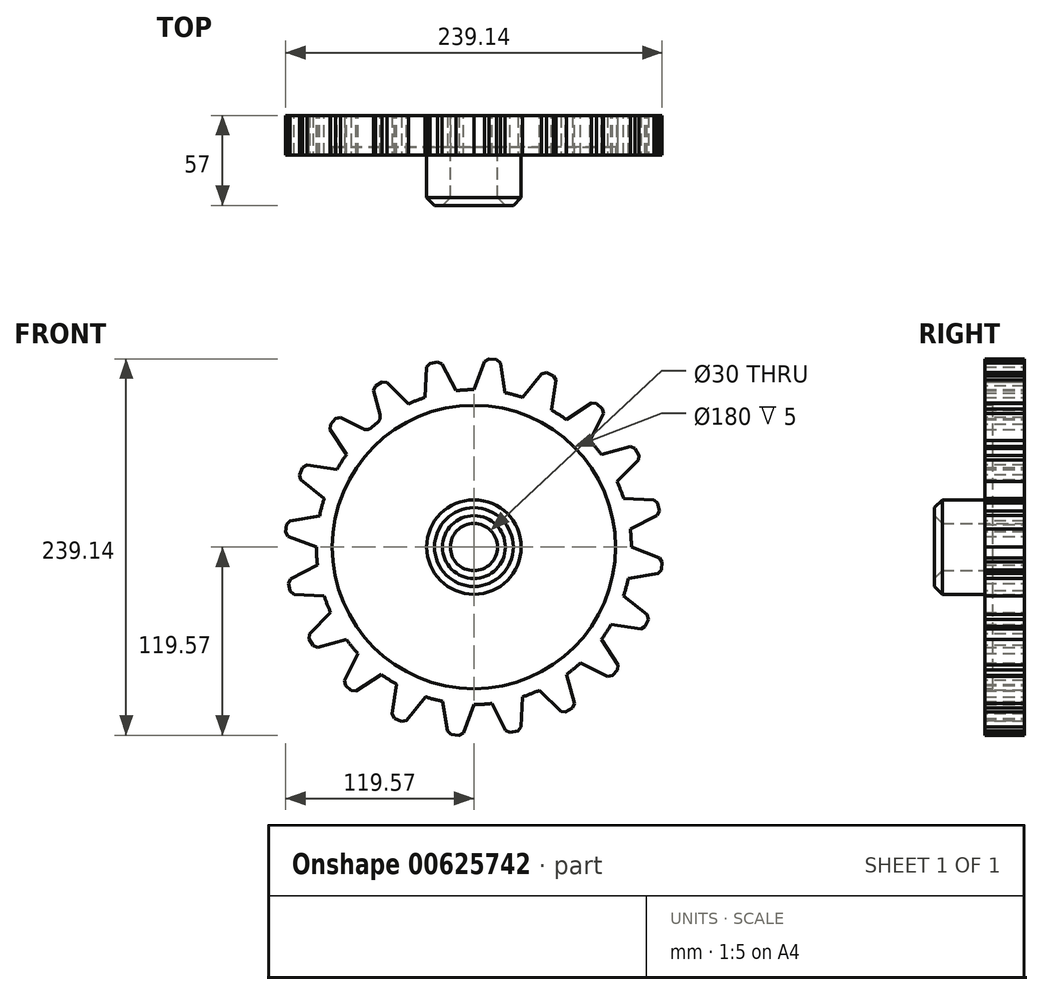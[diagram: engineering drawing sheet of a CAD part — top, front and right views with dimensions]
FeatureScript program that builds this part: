
annotation { "Feature Type Name" : "Feature", "Feature Type Description" : "" }
export const myFeature = defineFeature(function(context is Context, id is Id, definition is map)
    precondition{}
    {
        {
            var Q0;
            Q0=qCreatedBy(makeId("Front.planeOp"),FACE);
            var sketch = newSketch(context, id + "F0", { "sketchPlane" : qUnion([Q0])});
            skCircle(sketch, "E0", {"center": v(0, 0) * mm, "radius": 100 * mm});
            skCircle(sketch, "E1", {"center": v(0, 0) * mm, "radius": 120 * mm, "construction": true});
            skLineSegment(sketch, "E2", {"start": v(101.28, 64.36) * mm, "end": v(80.9, 58.79) * mm});
            skLineSegment(sketch, "E3", {"start": v(0, 0) * mm, "end": v(0, 0) * mm});
            skLineSegment(sketch, "E4.MirrorCS", {"start": v(105.82, 56.59) * mm, "end": v(90.95, 41.57) * mm});
            skLineSegment(sketch, "E5", {"start": v(101.28, 64.36) * mm, "end": v(105.82, 56.59) * mm});
            skLineSegment(sketch, "E6.1.0", {"start": v(76.44, 92.5) * mm, "end": v(58.77, 80.9) * mm});
            skLineSegment(sketch, "E6.1.1", {"start": v(76.44, 92.5) * mm, "end": v(83.15, 86.52) * mm});
            skLineSegment(sketch, "E6.1.2", {"start": v(83.15, 86.52) * mm, "end": v(73.65, 67.64) * mm});
            skLineSegment(sketch, "E6.2.0", {"start": v(44.1, 111.6) * mm, "end": v(30.89, 95.1) * mm});
            skLineSegment(sketch, "E6.2.1", {"start": v(44.1, 111.6) * mm, "end": v(52.35, 107.98) * mm});
            skLineSegment(sketch, "E6.2.2", {"start": v(52.35, 107.98) * mm, "end": v(49.15, 87.1) * mm});
            skLineSegment(sketch, "E7.2.3.0", {"start": v(7.46, 119.77) * mm, "end": v(-0.01, 100) * mm});
            skLineSegment(sketch, "E7.3.3.0", {"start": v(7.46, 119.77) * mm, "end": v(16.42, 118.87) * mm});
            skLineSegment(sketch, "E7.6.3.0", {"start": v(16.42, 118.87) * mm, "end": v(19.83, 98.01) * mm});
            skLineSegment(sketch, "E7.2.4.0", {"start": v(-29.91, 116.21) * mm, "end": v(-30.91, 95.1) * mm});
            skLineSegment(sketch, "E7.3.4.0", {"start": v(-29.91, 116.21) * mm, "end": v(-21.12, 118.13) * mm});
            skLineSegment(sketch, "E7.6.4.0", {"start": v(-21.12, 118.13) * mm, "end": v(-11.43, 99.34) * mm});
            skLineSegment(sketch, "E7.2.5.0", {"start": v(-64.36, 101.28) * mm, "end": v(-58.79, 80.9) * mm});
            skLineSegment(sketch, "E7.3.5.0", {"start": v(-64.36, 101.28) * mm, "end": v(-56.59, 105.82) * mm});
            skLineSegment(sketch, "E7.6.5.0", {"start": v(-56.59, 105.82) * mm, "end": v(-41.57, 90.95) * mm});
            skLineSegment(sketch, "E7.2.6.0", {"start": v(-92.5, 76.44) * mm, "end": v(-80.9, 58.77) * mm});
            skLineSegment(sketch, "E7.3.6.0", {"start": v(-92.5, 76.44) * mm, "end": v(-86.52, 83.15) * mm});
            skLineSegment(sketch, "E7.6.6.0", {"start": v(-86.52, 83.15) * mm, "end": v(-67.64, 73.65) * mm});
            skLineSegment(sketch, "E7.2.7.0", {"start": v(-111.6, 44.1) * mm, "end": v(-95.1, 30.89) * mm});
            skLineSegment(sketch, "E7.3.7.0", {"start": v(-111.6, 44.1) * mm, "end": v(-107.98, 52.35) * mm});
            skLineSegment(sketch, "E7.6.7.0", {"start": v(-107.98, 52.35) * mm, "end": v(-87.1, 49.15) * mm});
            skLineSegment(sketch, "E7.2.8.0", {"start": v(-119.77, 7.46) * mm, "end": v(-100, -0.01) * mm});
            skLineSegment(sketch, "E7.3.8.0", {"start": v(-119.77, 7.46) * mm, "end": v(-118.87, 16.42) * mm});
            skLineSegment(sketch, "E7.6.8.0", {"start": v(-118.87, 16.42) * mm, "end": v(-98.01, 19.83) * mm});
            skLineSegment(sketch, "E7.2.9.0", {"start": v(-116.21, -29.91) * mm, "end": v(-95.1, -30.91) * mm});
            skLineSegment(sketch, "E7.3.9.0", {"start": v(-116.21, -29.91) * mm, "end": v(-118.13, -21.12) * mm});
            skLineSegment(sketch, "E7.6.9.0", {"start": v(-118.13, -21.12) * mm, "end": v(-99.34, -11.43) * mm});
            skLineSegment(sketch, "E7.2.10.0", {"start": v(-101.28, -64.36) * mm, "end": v(-80.9, -58.79) * mm});
            skLineSegment(sketch, "E7.3.10.0", {"start": v(-101.28, -64.36) * mm, "end": v(-105.82, -56.59) * mm});
            skLineSegment(sketch, "E7.6.10.0", {"start": v(-105.82, -56.59) * mm, "end": v(-90.95, -41.57) * mm});
            skLineSegment(sketch, "E7.2.11.0", {"start": v(-76.44, -92.5) * mm, "end": v(-58.77, -80.9) * mm});
            skLineSegment(sketch, "E7.3.11.0", {"start": v(-76.44, -92.5) * mm, "end": v(-83.15, -86.52) * mm});
            skLineSegment(sketch, "E7.6.11.0", {"start": v(-83.15, -86.52) * mm, "end": v(-73.65, -67.64) * mm});
            skLineSegment(sketch, "E7.2.12.0", {"start": v(-44.1, -111.6) * mm, "end": v(-30.89, -95.1) * mm});
            skLineSegment(sketch, "E7.3.12.0", {"start": v(-44.1, -111.6) * mm, "end": v(-52.35, -107.98) * mm});
            skLineSegment(sketch, "E7.6.12.0", {"start": v(-52.35, -107.98) * mm, "end": v(-49.15, -87.1) * mm});
            skLineSegment(sketch, "E7.2.13.0", {"start": v(-7.46, -119.77) * mm, "end": v(0.01, -100) * mm});
            skLineSegment(sketch, "E7.3.13.0", {"start": v(-7.46, -119.77) * mm, "end": v(-16.42, -118.87) * mm});
            skLineSegment(sketch, "E7.6.13.0", {"start": v(-16.42, -118.87) * mm, "end": v(-19.83, -98.01) * mm});
            skLineSegment(sketch, "E7.2.14.0", {"start": v(29.91, -116.21) * mm, "end": v(30.91, -95.1) * mm});
            skLineSegment(sketch, "E7.3.14.0", {"start": v(29.91, -116.21) * mm, "end": v(21.12, -118.13) * mm});
            skLineSegment(sketch, "E7.6.14.0", {"start": v(21.12, -118.13) * mm, "end": v(11.43, -99.34) * mm});
            skLineSegment(sketch, "E7.2.15.0", {"start": v(64.36, -101.28) * mm, "end": v(58.79, -80.9) * mm});
            skLineSegment(sketch, "E7.3.15.0", {"start": v(64.36, -101.28) * mm, "end": v(56.59, -105.82) * mm});
            skLineSegment(sketch, "E7.6.15.0", {"start": v(56.59, -105.82) * mm, "end": v(41.57, -90.95) * mm});
            skLineSegment(sketch, "E7.2.16.0", {"start": v(92.5, -76.44) * mm, "end": v(80.9, -58.77) * mm});
            skLineSegment(sketch, "E7.3.16.0", {"start": v(92.5, -76.44) * mm, "end": v(86.52, -83.15) * mm});
            skLineSegment(sketch, "E7.6.16.0", {"start": v(86.52, -83.15) * mm, "end": v(67.64, -73.65) * mm});
            skLineSegment(sketch, "E7.2.17.0", {"start": v(111.6, -44.1) * mm, "end": v(95.1, -30.89) * mm});
            skLineSegment(sketch, "E7.3.17.0", {"start": v(111.6, -44.1) * mm, "end": v(107.98, -52.35) * mm});
            skLineSegment(sketch, "E7.6.17.0", {"start": v(107.98, -52.35) * mm, "end": v(87.1, -49.15) * mm});
            skLineSegment(sketch, "E7.2.18.0", {"start": v(119.77, -7.46) * mm, "end": v(100, 0.01) * mm});
            skLineSegment(sketch, "E7.3.18.0", {"start": v(119.77, -7.46) * mm, "end": v(118.87, -16.42) * mm});
            skLineSegment(sketch, "E7.6.18.0", {"start": v(118.87, -16.42) * mm, "end": v(98.01, -19.83) * mm});
            skLineSegment(sketch, "E7.2.19.0", {"start": v(116.21, 29.91) * mm, "end": v(95.1, 30.91) * mm});
            skLineSegment(sketch, "E7.3.19.0", {"start": v(116.21, 29.91) * mm, "end": v(118.13, 21.12) * mm});
            skLineSegment(sketch, "E7.6.19.0", {"start": v(118.13, 21.12) * mm, "end": v(99.34, 11.43) * mm});
            skSolve(sketch);
        }
        {
            var Q0;
            {var subQ0=sQuery(id+"F0.wireOp",EDGE,"E0");var subQ17=makeQuery(id+"F0.imprint","INTERSECT",VERTEX,{"derivedFrom":[sQuery(id+"F0.wireOp",EDGE,"E7.2.11.0"),subQ0]});Q0=makeQuery(id+"F0.imprint","IMPRINT",FACE,{"disambiguationData":[TD([[makeQuery(id+"F0.imprint","IMPRINT",EDGE,{"disambiguationData":[TD([[subQ17,1.0]])],"derivedFrom":subQ0}),1.0]])]});}
            var Q1;
            {var subQ0=sQuery(id+"F0.wireOp",EDGE,"E7.2.19.0");Q1=makeQuery(id+"F0.imprint","IMPRINT",FACE,{"disambiguationData":[TD([[makeQuery(id+"F0.imprint","IMPRINT",EDGE,{"derivedFrom":subQ0}),1.0]])]});}
            var Q2;
            {var subQ0=sQuery(id+"F0.wireOp",EDGE,"E7.2.15.0");Q2=makeQuery(id+"F0.imprint","IMPRINT",FACE,{"disambiguationData":[TD([[makeQuery(id+"F0.imprint","IMPRINT",EDGE,{"derivedFrom":subQ0}),1.0]])]});}
            var Q3;
            {var subQ0=sQuery(id+"F0.wireOp",EDGE,"E7.2.13.0");Q3=makeQuery(id+"F0.imprint","IMPRINT",FACE,{"disambiguationData":[TD([[makeQuery(id+"F0.imprint","IMPRINT",EDGE,{"derivedFrom":subQ0}),1.0]])]});}
            var Q4;
            {var subQ0=sQuery(id+"F0.wireOp",EDGE,"E7.2.14.0");Q4=makeQuery(id+"F0.imprint","IMPRINT",FACE,{"disambiguationData":[TD([[makeQuery(id+"F0.imprint","IMPRINT",EDGE,{"derivedFrom":subQ0}),1.0]])]});}
            var Q5;
            {var subQ0=sQuery(id+"F0.wireOp",EDGE,"E7.2.16.0");Q5=makeQuery(id+"F0.imprint","IMPRINT",FACE,{"disambiguationData":[TD([[makeQuery(id+"F0.imprint","IMPRINT",EDGE,{"derivedFrom":subQ0}),1.0]])]});}
            var Q6;
            {var subQ0=sQuery(id+"F0.wireOp",EDGE,"E2");Q6=makeQuery(id+"F0.imprint","IMPRINT",FACE,{"disambiguationData":[TD([[makeQuery(id+"F0.imprint","IMPRINT",EDGE,{"derivedFrom":subQ0}),1.0]])]});}
            var Q7;
            {var subQ0=sQuery(id+"F0.wireOp",EDGE,"E6.1.0");Q7=makeQuery(id+"F0.imprint","IMPRINT",FACE,{"disambiguationData":[TD([[makeQuery(id+"F0.imprint","IMPRINT",EDGE,{"derivedFrom":subQ0}),1.0]])]});}
            var Q8;
            {var subQ0=sQuery(id+"F0.wireOp",EDGE,"E6.2.0");Q8=makeQuery(id+"F0.imprint","IMPRINT",FACE,{"disambiguationData":[TD([[makeQuery(id+"F0.imprint","IMPRINT",EDGE,{"derivedFrom":subQ0}),1.0]])]});}
            var Q9;
            {var subQ0=sQuery(id+"F0.wireOp",EDGE,"E7.2.3.0");Q9=makeQuery(id+"F0.imprint","IMPRINT",FACE,{"disambiguationData":[TD([[makeQuery(id+"F0.imprint","IMPRINT",EDGE,{"derivedFrom":subQ0}),1.0]])]});}
            var Q10;
            {var subQ0=sQuery(id+"F0.wireOp",EDGE,"E7.2.4.0");Q10=makeQuery(id+"F0.imprint","IMPRINT",FACE,{"disambiguationData":[TD([[makeQuery(id+"F0.imprint","IMPRINT",EDGE,{"derivedFrom":subQ0}),1.0]])]});}
            var Q11;
            {var subQ0=sQuery(id+"F0.wireOp",EDGE,"E7.2.5.0");Q11=makeQuery(id+"F0.imprint","IMPRINT",FACE,{"disambiguationData":[TD([[makeQuery(id+"F0.imprint","IMPRINT",EDGE,{"derivedFrom":subQ0}),1.0]])]});}
            var Q12;
            {var subQ0=sQuery(id+"F0.wireOp",EDGE,"E7.2.6.0");Q12=makeQuery(id+"F0.imprint","IMPRINT",FACE,{"disambiguationData":[TD([[makeQuery(id+"F0.imprint","IMPRINT",EDGE,{"derivedFrom":subQ0}),1.0]])]});}
            var Q13;
            {var subQ0=sQuery(id+"F0.wireOp",EDGE,"E7.2.7.0");Q13=makeQuery(id+"F0.imprint","IMPRINT",FACE,{"disambiguationData":[TD([[makeQuery(id+"F0.imprint","IMPRINT",EDGE,{"derivedFrom":subQ0}),1.0]])]});}
            var Q14;
            {var subQ0=sQuery(id+"F0.wireOp",EDGE,"E7.2.8.0");Q14=makeQuery(id+"F0.imprint","IMPRINT",FACE,{"disambiguationData":[TD([[makeQuery(id+"F0.imprint","IMPRINT",EDGE,{"derivedFrom":subQ0}),1.0]])]});}
            var Q15;
            {var subQ0=sQuery(id+"F0.wireOp",EDGE,"E7.2.9.0");Q15=makeQuery(id+"F0.imprint","IMPRINT",FACE,{"disambiguationData":[TD([[makeQuery(id+"F0.imprint","IMPRINT",EDGE,{"derivedFrom":subQ0}),1.0]])]});}
            var Q16;
            {var subQ0=sQuery(id+"F0.wireOp",EDGE,"E7.2.10.0");Q16=makeQuery(id+"F0.imprint","IMPRINT",FACE,{"disambiguationData":[TD([[makeQuery(id+"F0.imprint","IMPRINT",EDGE,{"derivedFrom":subQ0}),1.0]])]});}
            var Q17;
            {var subQ0=sQuery(id+"F0.wireOp",EDGE,"E7.2.11.0");Q17=makeQuery(id+"F0.imprint","IMPRINT",FACE,{"disambiguationData":[TD([[makeQuery(id+"F0.imprint","IMPRINT",EDGE,{"derivedFrom":subQ0}),1.0]])]});}
            var Q18;
            {var subQ0=sQuery(id+"F0.wireOp",EDGE,"E7.2.12.0");Q18=makeQuery(id+"F0.imprint","IMPRINT",FACE,{"disambiguationData":[TD([[makeQuery(id+"F0.imprint","IMPRINT",EDGE,{"derivedFrom":subQ0}),1.0]])]});}
            var Q19;
            {var subQ0=sQuery(id+"F0.wireOp",EDGE,"E7.2.17.0");Q19=makeQuery(id+"F0.imprint","IMPRINT",FACE,{"disambiguationData":[TD([[makeQuery(id+"F0.imprint","IMPRINT",EDGE,{"derivedFrom":subQ0}),1.0]])]});}
            var Q20;
            {var subQ0=sQuery(id+"F0.wireOp",EDGE,"E7.2.18.0");Q20=makeQuery(id+"F0.imprint","IMPRINT",FACE,{"disambiguationData":[TD([[makeQuery(id+"F0.imprint","IMPRINT",EDGE,{"derivedFrom":subQ0}),1.0]])]});}
            extrude(context, id + "F1", {"entities" : qUnion([Q0, Q1, Q2, Q3, Q4, Q5, Q6, Q7, Q8, Q9, Q10, Q11, Q12, Q13, Q14, Q15, Q16, Q17, Q18, Q19, Q20]), "depth" : 25 * mm, "offsetDistance" : 25 * mm});
        }
        {
            var Q0;
            Q0=makeQuery(id+"F1.opExtrude","SWEPT_EDGE",EDGE,{"disambiguationData":[OSD([sQuery(id+"F0.wireOp",EDGE,"E7.6.6.0"),sQuery(id+"F0.wireOp",EDGE,"E0")])]});
            fillet(context, id + "F2", {"entities" : qUnion([Q0]), "radius" : 5 * mm, "tangentPropagation" : true, "allowEdgeOverflow" : false});
        }
        {
            var Q0;
            Q0=makeQuery(id+"F1.opExtrude","SWEPT_EDGE",EDGE,{"disambiguationData":[OSD([sQuery(id+"F0.wireOp",EDGE,"E7.2.5.0"),sQuery(id+"F0.wireOp",EDGE,"E0")])]});
            fillet(context, id + "F3", {"entities" : qUnion([Q0]), "radius" : 5 * mm, "tangentPropagation" : true, "allowEdgeOverflow" : false});
        }
        {
            var Q0;
            Q0=makeQuery(id+"F1.opExtrude","CAP_FACE",FACE,{"disambiguationData":[OSD([sQuery(id+"F0.wireOp",EDGE,"E2"),sQuery(id+"F0.wireOp",EDGE,"E4.MirrorCS"),sQuery(id+"F0.wireOp",EDGE,"E5"),sQuery(id+"F0.wireOp",EDGE,"E6.1.0"),sQuery(id+"F0.wireOp",EDGE,"E6.1.1"),sQuery(id+"F0.wireOp",EDGE,"E6.1.2"),sQuery(id+"F0.wireOp",EDGE,"E6.2.0"),sQuery(id+"F0.wireOp",EDGE,"E6.2.1"),sQuery(id+"F0.wireOp",EDGE,"E6.2.2"),sQuery(id+"F0.wireOp",EDGE,"E7.2.3.0"),sQuery(id+"F0.wireOp",EDGE,"E7.3.3.0"),sQuery(id+"F0.wireOp",EDGE,"E7.6.3.0"),sQuery(id+"F0.wireOp",EDGE,"E7.2.4.0"),sQuery(id+"F0.wireOp",EDGE,"E7.3.4.0"),sQuery(id+"F0.wireOp",EDGE,"E7.6.4.0"),sQuery(id+"F0.wireOp",EDGE,"E7.2.5.0"),sQuery(id+"F0.wireOp",EDGE,"E7.3.5.0"),sQuery(id+"F0.wireOp",EDGE,"E7.6.5.0"),sQuery(id+"F0.wireOp",EDGE,"E7.2.6.0"),sQuery(id+"F0.wireOp",EDGE,"E7.3.6.0"),sQuery(id+"F0.wireOp",EDGE,"E7.6.6.0"),sQuery(id+"F0.wireOp",EDGE,"E7.2.7.0"),sQuery(id+"F0.wireOp",EDGE,"E7.3.7.0"),sQuery(id+"F0.wireOp",EDGE,"E7.6.7.0"),sQuery(id+"F0.wireOp",EDGE,"E7.2.8.0"),sQuery(id+"F0.wireOp",EDGE,"E7.3.8.0"),sQuery(id+"F0.wireOp",EDGE,"E7.6.8.0"),sQuery(id+"F0.wireOp",EDGE,"E7.2.9.0"),sQuery(id+"F0.wireOp",EDGE,"E7.3.9.0"),sQuery(id+"F0.wireOp",EDGE,"E7.6.9.0"),sQuery(id+"F0.wireOp",EDGE,"E7.2.10.0"),sQuery(id+"F0.wireOp",EDGE,"E7.3.10.0"),sQuery(id+"F0.wireOp",EDGE,"E7.6.10.0"),sQuery(id+"F0.wireOp",EDGE,"E7.2.11.0"),sQuery(id+"F0.wireOp",EDGE,"E7.3.11.0"),sQuery(id+"F0.wireOp",EDGE,"E7.6.11.0"),sQuery(id+"F0.wireOp",EDGE,"E7.2.12.0"),sQuery(id+"F0.wireOp",EDGE,"E7.3.12.0"),sQuery(id+"F0.wireOp",EDGE,"E7.6.12.0"),sQuery(id+"F0.wireOp",EDGE,"E7.2.13.0"),sQuery(id+"F0.wireOp",EDGE,"E7.3.13.0"),sQuery(id+"F0.wireOp",EDGE,"E7.6.13.0"),sQuery(id+"F0.wireOp",EDGE,"E7.2.14.0"),sQuery(id+"F0.wireOp",EDGE,"E7.3.14.0"),sQuery(id+"F0.wireOp",EDGE,"E7.6.14.0"),sQuery(id+"F0.wireOp",EDGE,"E7.2.15.0"),sQuery(id+"F0.wireOp",EDGE,"E7.3.15.0"),sQuery(id+"F0.wireOp",EDGE,"E7.6.15.0"),sQuery(id+"F0.wireOp",EDGE,"E7.2.16.0"),sQuery(id+"F0.wireOp",EDGE,"E7.3.16.0"),sQuery(id+"F0.wireOp",EDGE,"E7.6.16.0"),sQuery(id+"F0.wireOp",EDGE,"E7.2.17.0"),sQuery(id+"F0.wireOp",EDGE,"E7.3.17.0"),sQuery(id+"F0.wireOp",EDGE,"E7.6.17.0"),sQuery(id+"F0.wireOp",EDGE,"E7.2.18.0"),sQuery(id+"F0.wireOp",EDGE,"E7.3.18.0"),sQuery(id+"F0.wireOp",EDGE,"E7.6.18.0"),sQuery(id+"F0.wireOp",EDGE,"E7.2.19.0"),sQuery(id+"F0.wireOp",EDGE,"E7.3.19.0"),sQuery(id+"F0.wireOp",EDGE,"E7.6.19.0"),sQuery(id+"F0.wireOp",EDGE,"E0")])],"isStart":false});
            var sketch = newSketch(context, id + "F4", { "sketchPlane" : qUnion([Q0])});
            skCircle(sketch, "E8", {"center": v(0, 0) * mm, "radius": 90 * mm});
            skCircle(sketch, "E9", {"center": v(0, 0) * mm, "radius": 30 * mm});
            skCircle(sketch, "E10", {"center": v(0, 0) * mm, "radius": 15 * mm});
            skSolve(sketch);
        }
        {
            var Q0;
            Q0=makeQuery(id+"F4.imprint","IMPRINT",FACE,{"disambiguationData":[TD([[makeQuery(id+"F4.imprint","IMPRINT",EDGE,{"derivedFrom":sQuery(id+"F4.wireOp",EDGE,"E9")}),1.0]])]});
            extrude(context, id + "F5", {"entities" : qUnion([Q0]), "operationType" : NewBodyOperationType.ADD, "depth" : 32 * mm, "offsetDistance" : 25 * mm});
        }
        {
            var Q0;
            Q0=makeQuery(id+"F5.boolean.opBoolean","SPLIT",FACE,{"disambiguationData":[TD([makeQuery(id+"F5.opExtrude","SWEPT_FACE",FACE,{"disambiguationData":[OSD([sQuery(id+"F4.wireOp",EDGE,"E10")])]})])],"derivedFrom":makeQuery(id+"F1.opExtrude","CAP_FACE",FACE,{"disambiguationData":[OSD([sQuery(id+"F0.wireOp",EDGE,"E2"),sQuery(id+"F0.wireOp",EDGE,"E4.MirrorCS"),sQuery(id+"F0.wireOp",EDGE,"E5"),sQuery(id+"F0.wireOp",EDGE,"E6.1.0"),sQuery(id+"F0.wireOp",EDGE,"E6.1.1"),sQuery(id+"F0.wireOp",EDGE,"E6.1.2"),sQuery(id+"F0.wireOp",EDGE,"E6.2.0"),sQuery(id+"F0.wireOp",EDGE,"E6.2.1"),sQuery(id+"F0.wireOp",EDGE,"E6.2.2"),sQuery(id+"F0.wireOp",EDGE,"E7.2.3.0"),sQuery(id+"F0.wireOp",EDGE,"E7.3.3.0"),sQuery(id+"F0.wireOp",EDGE,"E7.6.3.0"),sQuery(id+"F0.wireOp",EDGE,"E7.2.4.0"),sQuery(id+"F0.wireOp",EDGE,"E7.3.4.0"),sQuery(id+"F0.wireOp",EDGE,"E7.6.4.0"),sQuery(id+"F0.wireOp",EDGE,"E7.2.5.0"),sQuery(id+"F0.wireOp",EDGE,"E7.3.5.0"),sQuery(id+"F0.wireOp",EDGE,"E7.6.5.0"),sQuery(id+"F0.wireOp",EDGE,"E7.2.6.0"),sQuery(id+"F0.wireOp",EDGE,"E7.3.6.0"),sQuery(id+"F0.wireOp",EDGE,"E7.6.6.0"),sQuery(id+"F0.wireOp",EDGE,"E7.2.7.0"),sQuery(id+"F0.wireOp",EDGE,"E7.3.7.0"),sQuery(id+"F0.wireOp",EDGE,"E7.6.7.0"),sQuery(id+"F0.wireOp",EDGE,"E7.2.8.0"),sQuery(id+"F0.wireOp",EDGE,"E7.3.8.0"),sQuery(id+"F0.wireOp",EDGE,"E7.6.8.0"),sQuery(id+"F0.wireOp",EDGE,"E7.2.9.0"),sQuery(id+"F0.wireOp",EDGE,"E7.3.9.0"),sQuery(id+"F0.wireOp",EDGE,"E7.6.9.0"),sQuery(id+"F0.wireOp",EDGE,"E7.2.10.0"),sQuery(id+"F0.wireOp",EDGE,"E7.3.10.0"),sQuery(id+"F0.wireOp",EDGE,"E7.6.10.0"),sQuery(id+"F0.wireOp",EDGE,"E7.2.11.0"),sQuery(id+"F0.wireOp",EDGE,"E7.3.11.0"),sQuery(id+"F0.wireOp",EDGE,"E7.6.11.0"),sQuery(id+"F0.wireOp",EDGE,"E7.2.12.0"),sQuery(id+"F0.wireOp",EDGE,"E7.3.12.0"),sQuery(id+"F0.wireOp",EDGE,"E7.6.12.0"),sQuery(id+"F0.wireOp",EDGE,"E7.2.13.0"),sQuery(id+"F0.wireOp",EDGE,"E7.3.13.0"),sQuery(id+"F0.wireOp",EDGE,"E7.6.13.0"),sQuery(id+"F0.wireOp",EDGE,"E7.2.14.0"),sQuery(id+"F0.wireOp",EDGE,"E7.3.14.0"),sQuery(id+"F0.wireOp",EDGE,"E7.6.14.0"),sQuery(id+"F0.wireOp",EDGE,"E7.2.15.0"),sQuery(id+"F0.wireOp",EDGE,"E7.3.15.0"),sQuery(id+"F0.wireOp",EDGE,"E7.6.15.0"),sQuery(id+"F0.wireOp",EDGE,"E7.2.16.0"),sQuery(id+"F0.wireOp",EDGE,"E7.3.16.0"),sQuery(id+"F0.wireOp",EDGE,"E7.6.16.0"),sQuery(id+"F0.wireOp",EDGE,"E7.2.17.0"),sQuery(id+"F0.wireOp",EDGE,"E7.3.17.0"),sQuery(id+"F0.wireOp",EDGE,"E7.6.17.0"),sQuery(id+"F0.wireOp",EDGE,"E7.2.18.0"),sQuery(id+"F0.wireOp",EDGE,"E7.3.18.0"),sQuery(id+"F0.wireOp",EDGE,"E7.6.18.0"),sQuery(id+"F0.wireOp",EDGE,"E7.2.19.0"),sQuery(id+"F0.wireOp",EDGE,"E7.3.19.0"),sQuery(id+"F0.wireOp",EDGE,"E7.6.19.0"),sQuery(id+"F0.wireOp",EDGE,"E0")])],"isStart":false})});
            extrude(context, id + "F6", {"entities" : qUnion([Q0]), "operationType" : NewBodyOperationType.REMOVE, "endBound" : BoundingType.THROUGH_ALL, "oppositeDirection" : true, "depth" : 25 * mm, "offsetDistance" : 25 * mm});
        }
        {
            var Q0;
            Q0=makeQuery(id+"F5.opExtrude","CAP_EDGE",EDGE,{"disambiguationData":[OSD([sQuery(id+"F4.wireOp",EDGE,"E9")])],"isStart":false});
            chamfer(context, id + "F7", {"entities" : qUnion([Q0]), "width" : 5 * mm, "tangentPropagation" : true});
        }
        {
            var Q0;
            Q0=makeQuery(id+"F5.opExtrude","CAP_EDGE",EDGE,{"disambiguationData":[OSD([sQuery(id+"F4.wireOp",EDGE,"E10")])],"isStart":false});
            chamfer(context, id + "F8", {"entities" : qUnion([Q0]), "width" : 5 * mm, "tangentPropagation" : true});
        }
        {
            var Q0;
            Q0=makeQuery(id+"F4.imprint","IMPRINT",FACE,{"disambiguationData":[TD([[makeQuery(id+"F4.imprint","IMPRINT",EDGE,{"derivedFrom":sQuery(id+"F4.wireOp",EDGE,"E8")}),1.0]])]});
            extrude(context, id + "F9", {"entities" : qUnion([Q0]), "operationType" : NewBodyOperationType.REMOVE, "oppositeDirection" : true, "depth" : 5 * mm, "offsetDistance" : 25 * mm});
        }
        {
            var Q0;
            Q0=makeQuery(id+"F1.opExtrude","SWEPT_EDGE",EDGE,{"disambiguationData":[OSD([sQuery(id+"F0.wireOp",EDGE,"E7.3.10.0"),sQuery(id+"F0.wireOp",EDGE,"E7.6.10.0")])]});
            var Q1;
            Q1=makeQuery(id+"F1.opExtrude","SWEPT_EDGE",EDGE,{"disambiguationData":[OSD([sQuery(id+"F0.wireOp",EDGE,"E7.2.10.0"),sQuery(id+"F0.wireOp",EDGE,"E7.3.10.0")])]});
            var Q2;
            Q2=makeQuery(id+"F1.opExtrude","SWEPT_EDGE",EDGE,{"disambiguationData":[OSD([sQuery(id+"F0.wireOp",EDGE,"E7.3.11.0"),sQuery(id+"F0.wireOp",EDGE,"E7.6.11.0")])]});
            var Q3;
            Q3=makeQuery(id+"F1.opExtrude","SWEPT_EDGE",EDGE,{"disambiguationData":[OSD([sQuery(id+"F0.wireOp",EDGE,"E7.2.11.0"),sQuery(id+"F0.wireOp",EDGE,"E7.3.11.0")])]});
            var Q4;
            Q4=makeQuery(id+"F1.opExtrude","SWEPT_EDGE",EDGE,{"disambiguationData":[OSD([sQuery(id+"F0.wireOp",EDGE,"E7.3.12.0"),sQuery(id+"F0.wireOp",EDGE,"E7.6.12.0")])]});
            var Q5;
            Q5=makeQuery(id+"F1.opExtrude","SWEPT_EDGE",EDGE,{"disambiguationData":[OSD([sQuery(id+"F0.wireOp",EDGE,"E7.2.12.0"),sQuery(id+"F0.wireOp",EDGE,"E7.3.12.0")])]});
            var Q6;
            Q6=makeQuery(id+"F1.opExtrude","SWEPT_EDGE",EDGE,{"disambiguationData":[OSD([sQuery(id+"F0.wireOp",EDGE,"E7.3.13.0"),sQuery(id+"F0.wireOp",EDGE,"E7.6.13.0")])]});
            var Q7;
            Q7=makeQuery(id+"F1.opExtrude","SWEPT_EDGE",EDGE,{"disambiguationData":[OSD([sQuery(id+"F0.wireOp",EDGE,"E7.2.13.0"),sQuery(id+"F0.wireOp",EDGE,"E7.3.13.0")])]});
            var Q8;
            Q8=makeQuery(id+"F1.opExtrude","SWEPT_EDGE",EDGE,{"disambiguationData":[OSD([sQuery(id+"F0.wireOp",EDGE,"E7.3.14.0"),sQuery(id+"F0.wireOp",EDGE,"E7.6.14.0")])]});
            var Q9;
            Q9=makeQuery(id+"F1.opExtrude","SWEPT_EDGE",EDGE,{"disambiguationData":[OSD([sQuery(id+"F0.wireOp",EDGE,"E7.2.14.0"),sQuery(id+"F0.wireOp",EDGE,"E7.3.14.0")])]});
            var Q10;
            Q10=makeQuery(id+"F1.opExtrude","SWEPT_EDGE",EDGE,{"disambiguationData":[OSD([sQuery(id+"F0.wireOp",EDGE,"E7.3.15.0"),sQuery(id+"F0.wireOp",EDGE,"E7.6.15.0")])]});
            var Q11;
            Q11=makeQuery(id+"F1.opExtrude","SWEPT_EDGE",EDGE,{"disambiguationData":[OSD([sQuery(id+"F0.wireOp",EDGE,"E7.2.15.0"),sQuery(id+"F0.wireOp",EDGE,"E7.3.15.0")])]});
            var Q12;
            Q12=makeQuery(id+"F1.opExtrude","SWEPT_EDGE",EDGE,{"disambiguationData":[OSD([sQuery(id+"F0.wireOp",EDGE,"E7.3.16.0"),sQuery(id+"F0.wireOp",EDGE,"E7.6.16.0")])]});
            var Q13;
            Q13=makeQuery(id+"F1.opExtrude","SWEPT_EDGE",EDGE,{"disambiguationData":[OSD([sQuery(id+"F0.wireOp",EDGE,"E7.2.16.0"),sQuery(id+"F0.wireOp",EDGE,"E7.3.16.0")])]});
            var Q14;
            Q14=makeQuery(id+"F1.opExtrude","SWEPT_EDGE",EDGE,{"disambiguationData":[OSD([sQuery(id+"F0.wireOp",EDGE,"E7.3.17.0"),sQuery(id+"F0.wireOp",EDGE,"E7.6.17.0")])]});
            var Q15;
            Q15=makeQuery(id+"F1.opExtrude","SWEPT_EDGE",EDGE,{"disambiguationData":[OSD([sQuery(id+"F0.wireOp",EDGE,"E7.2.17.0"),sQuery(id+"F0.wireOp",EDGE,"E7.3.17.0")])]});
            var Q16;
            Q16=makeQuery(id+"F1.opExtrude","SWEPT_EDGE",EDGE,{"disambiguationData":[OSD([sQuery(id+"F0.wireOp",EDGE,"E7.3.18.0"),sQuery(id+"F0.wireOp",EDGE,"E7.6.18.0")])]});
            var Q17;
            Q17=makeQuery(id+"F1.opExtrude","SWEPT_EDGE",EDGE,{"disambiguationData":[OSD([sQuery(id+"F0.wireOp",EDGE,"E7.2.18.0"),sQuery(id+"F0.wireOp",EDGE,"E7.3.18.0")])]});
            var Q18;
            Q18=makeQuery(id+"F1.opExtrude","SWEPT_EDGE",EDGE,{"disambiguationData":[OSD([sQuery(id+"F0.wireOp",EDGE,"E7.3.19.0"),sQuery(id+"F0.wireOp",EDGE,"E7.6.19.0")])]});
            var Q19;
            Q19=makeQuery(id+"F1.opExtrude","SWEPT_EDGE",EDGE,{"disambiguationData":[OSD([sQuery(id+"F0.wireOp",EDGE,"E7.2.19.0"),sQuery(id+"F0.wireOp",EDGE,"E7.3.19.0")])]});
            var Q20;
            Q20=makeQuery(id+"F1.opExtrude","SWEPT_EDGE",EDGE,{"disambiguationData":[OSD([sQuery(id+"F0.wireOp",EDGE,"E4.MirrorCS"),sQuery(id+"F0.wireOp",EDGE,"E5")])]});
            var Q21;
            Q21=makeQuery(id+"F1.opExtrude","SWEPT_EDGE",EDGE,{"disambiguationData":[OSD([sQuery(id+"F0.wireOp",EDGE,"E2"),sQuery(id+"F0.wireOp",EDGE,"E5")])]});
            var Q22;
            Q22=makeQuery(id+"F1.opExtrude","SWEPT_EDGE",EDGE,{"disambiguationData":[OSD([sQuery(id+"F0.wireOp",EDGE,"E6.1.1"),sQuery(id+"F0.wireOp",EDGE,"E6.1.2")])]});
            var Q23;
            Q23=makeQuery(id+"F1.opExtrude","SWEPT_EDGE",EDGE,{"disambiguationData":[OSD([sQuery(id+"F0.wireOp",EDGE,"E6.1.0"),sQuery(id+"F0.wireOp",EDGE,"E6.1.1")])]});
            var Q24;
            Q24=makeQuery(id+"F1.opExtrude","SWEPT_EDGE",EDGE,{"disambiguationData":[OSD([sQuery(id+"F0.wireOp",EDGE,"E6.2.1"),sQuery(id+"F0.wireOp",EDGE,"E6.2.2")])]});
            var Q25;
            Q25=makeQuery(id+"F1.opExtrude","SWEPT_EDGE",EDGE,{"disambiguationData":[OSD([sQuery(id+"F0.wireOp",EDGE,"E6.2.0"),sQuery(id+"F0.wireOp",EDGE,"E6.2.1")])]});
            var Q26;
            Q26=makeQuery(id+"F1.opExtrude","SWEPT_EDGE",EDGE,{"disambiguationData":[OSD([sQuery(id+"F0.wireOp",EDGE,"E7.3.3.0"),sQuery(id+"F0.wireOp",EDGE,"E7.6.3.0")])]});
            var Q27;
            Q27=makeQuery(id+"F1.opExtrude","SWEPT_EDGE",EDGE,{"disambiguationData":[OSD([sQuery(id+"F0.wireOp",EDGE,"E7.2.3.0"),sQuery(id+"F0.wireOp",EDGE,"E7.3.3.0")])]});
            var Q28;
            Q28=makeQuery(id+"F1.opExtrude","SWEPT_EDGE",EDGE,{"disambiguationData":[OSD([sQuery(id+"F0.wireOp",EDGE,"E7.3.4.0"),sQuery(id+"F0.wireOp",EDGE,"E7.6.4.0")])]});
            var Q29;
            Q29=makeQuery(id+"F1.opExtrude","SWEPT_EDGE",EDGE,{"disambiguationData":[OSD([sQuery(id+"F0.wireOp",EDGE,"E7.2.4.0"),sQuery(id+"F0.wireOp",EDGE,"E7.3.4.0")])]});
            var Q30;
            Q30=makeQuery(id+"F1.opExtrude","SWEPT_EDGE",EDGE,{"disambiguationData":[OSD([sQuery(id+"F0.wireOp",EDGE,"E7.3.5.0"),sQuery(id+"F0.wireOp",EDGE,"E7.6.5.0")])]});
            var Q31;
            Q31=makeQuery(id+"F1.opExtrude","SWEPT_EDGE",EDGE,{"disambiguationData":[OSD([sQuery(id+"F0.wireOp",EDGE,"E7.2.5.0"),sQuery(id+"F0.wireOp",EDGE,"E7.3.5.0")])]});
            var Q32;
            Q32=makeQuery(id+"F1.opExtrude","SWEPT_EDGE",EDGE,{"disambiguationData":[OSD([sQuery(id+"F0.wireOp",EDGE,"E7.3.6.0"),sQuery(id+"F0.wireOp",EDGE,"E7.6.6.0")])]});
            var Q33;
            Q33=makeQuery(id+"F1.opExtrude","SWEPT_EDGE",EDGE,{"disambiguationData":[OSD([sQuery(id+"F0.wireOp",EDGE,"E7.2.6.0"),sQuery(id+"F0.wireOp",EDGE,"E7.3.6.0")])]});
            var Q34;
            Q34=makeQuery(id+"F1.opExtrude","SWEPT_EDGE",EDGE,{"disambiguationData":[OSD([sQuery(id+"F0.wireOp",EDGE,"E7.3.7.0"),sQuery(id+"F0.wireOp",EDGE,"E7.6.7.0")])]});
            var Q35;
            Q35=makeQuery(id+"F1.opExtrude","SWEPT_EDGE",EDGE,{"disambiguationData":[OSD([sQuery(id+"F0.wireOp",EDGE,"E7.2.7.0"),sQuery(id+"F0.wireOp",EDGE,"E7.3.7.0")])]});
            var Q36;
            Q36=makeQuery(id+"F1.opExtrude","SWEPT_EDGE",EDGE,{"disambiguationData":[OSD([sQuery(id+"F0.wireOp",EDGE,"E7.3.8.0"),sQuery(id+"F0.wireOp",EDGE,"E7.6.8.0")])]});
            var Q37;
            Q37=makeQuery(id+"F1.opExtrude","SWEPT_EDGE",EDGE,{"disambiguationData":[OSD([sQuery(id+"F0.wireOp",EDGE,"E7.2.8.0"),sQuery(id+"F0.wireOp",EDGE,"E7.3.8.0")])]});
            var Q38;
            Q38=makeQuery(id+"F1.opExtrude","SWEPT_EDGE",EDGE,{"disambiguationData":[OSD([sQuery(id+"F0.wireOp",EDGE,"E7.3.9.0"),sQuery(id+"F0.wireOp",EDGE,"E7.6.9.0")])]});
            var Q39;
            Q39=makeQuery(id+"F1.opExtrude","SWEPT_EDGE",EDGE,{"disambiguationData":[OSD([sQuery(id+"F0.wireOp",EDGE,"E7.2.9.0"),sQuery(id+"F0.wireOp",EDGE,"E7.3.9.0")])]});
            chamfer(context, id + "F10", {"entities" : qUnion([Q0, Q1, Q2, Q3, Q4, Q5, Q6, Q7, Q8, Q9, Q10, Q11, Q12, Q13, Q14, Q15, Q16, Q17, Q18, Q19, Q20, Q21, Q22, Q23, Q24, Q25, Q26, Q27, Q28, Q29, Q30, Q31, Q32, Q33, Q34, Q35, Q36, Q37, Q38, Q39]), "chamferType" : ChamferType.TWO_OFFSETS, "width1" : 2 * mm, "oppositeDirection" : false, "width2" : 2 * mm, "tangentPropagation" : true});
        }
    });
